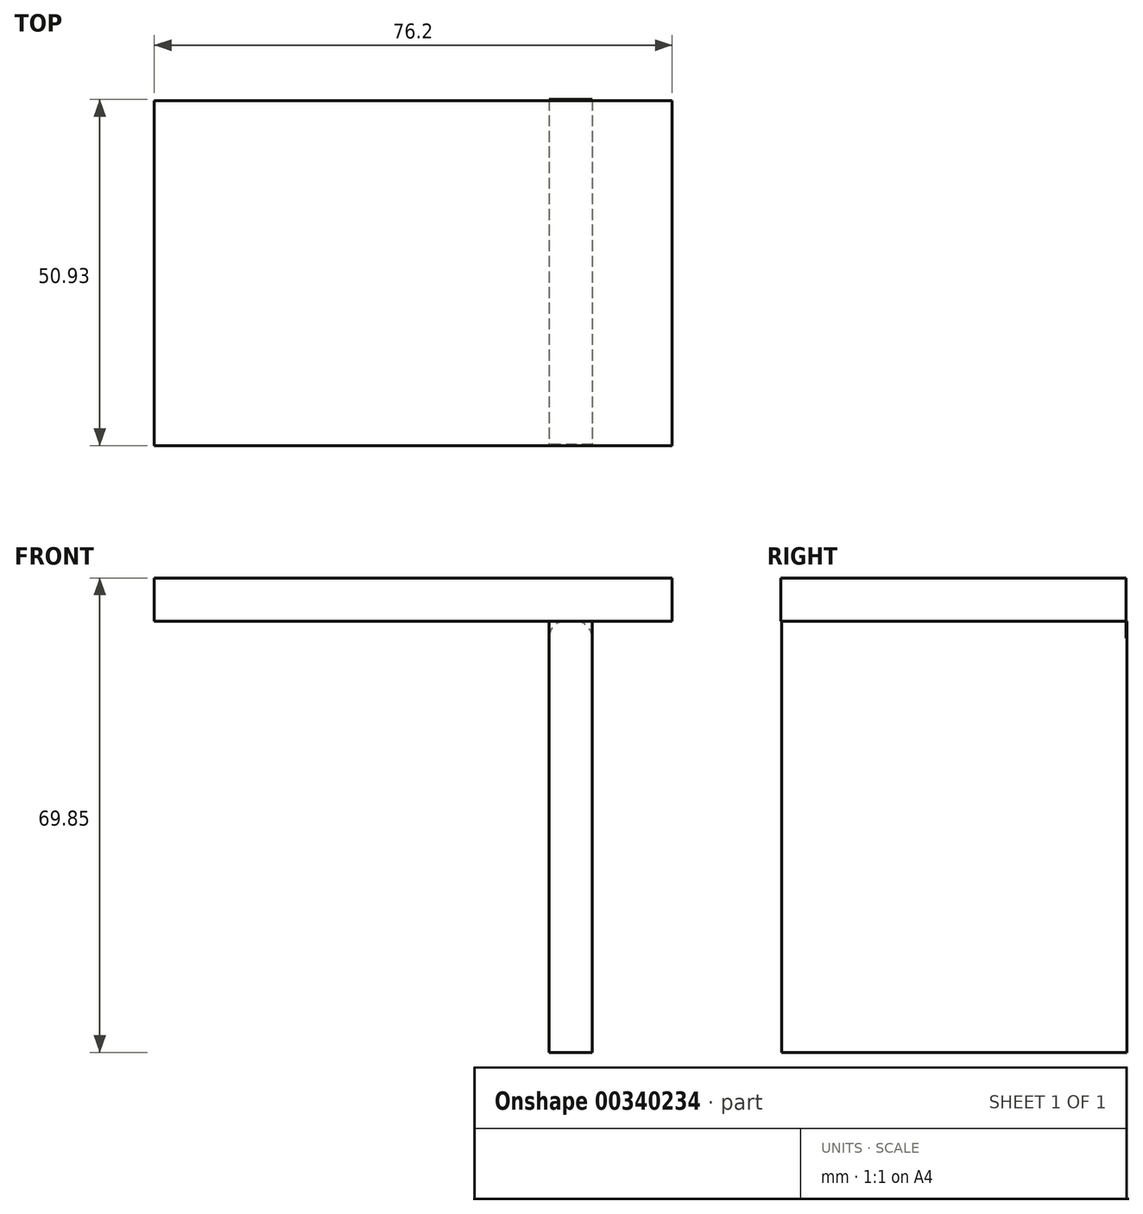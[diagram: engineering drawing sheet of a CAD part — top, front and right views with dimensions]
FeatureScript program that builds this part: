
annotation { "Feature Type Name" : "Feature", "Feature Type Description" : "" }
export const myFeature = defineFeature(function(context is Context, id is Id, definition is map)
    precondition{}
    {
        {
            var Q0;
            Q0=qCreatedBy(makeId("Top.planeOp"),FACE);
            var sketch = newSketch(context, id + "F0", { "sketchPlane" : qUnion([Q0])});
            skLineSegment(sketch, "E0.bottom", {"start": v(-37.07, 16.44) * mm, "end": v(39.13, 16.44) * mm});
            skLineSegment(sketch, "E0.top", {"start": v(-37.07, -34.36) * mm, "end": v(39.13, -34.36) * mm});
            skLineSegment(sketch, "E0.left", {"start": v(-37.07, 16.44) * mm, "end": v(-37.07, -34.36) * mm});
            skLineSegment(sketch, "E0.right", {"start": v(39.13, 16.44) * mm, "end": v(39.13, -34.36) * mm});
            skSolve(sketch);
        }
        {
            var Q0;
            Q0 = qSketchRegion(id + "F0", true);
            extrude(context, id + "F1", {"entities" : qUnion([Q0]), "depth" : 6.35 * mm});
        }
        {
            var Q0;
            Q0=qCreatedBy(makeId("Right.planeOp"),FACE);
            cPlane(context, id + "F2", {"entities" : qUnion([Q0]), "cplaneType" : CPlaneType.OFFSET, "offset" : 21 * mm, "width" : 150 * mm, "height" : 150 * mm});
        }
        {
            var Q0;
            Q0=qCreatedBy(id+"F2.planeOp",FACE);
            var sketch = newSketch(context, id + "F3", { "sketchPlane" : qUnion([Q0])});
            skLineSegment(sketch, "E1.bottom", {"start": v(16.57, 0) * mm, "end": v(-34.23, 0) * mm});
            skLineSegment(sketch, "E1.top", {"start": v(16.57, -63.5) * mm, "end": v(-34.23, -63.5) * mm});
            skLineSegment(sketch, "E1.left", {"start": v(16.57, 0) * mm, "end": v(16.57, -63.5) * mm});
            skLineSegment(sketch, "E1.right", {"start": v(-34.23, 0) * mm, "end": v(-34.23, -63.5) * mm});
            skSolve(sketch);
        }
        {
            var Q0;
            Q0 = qSketchRegion(id + "F3", true);
            extrude(context, id + "F4", {"entities" : qUnion([Q0]), "operationType" : NewBodyOperationType.ADD, "depth" : 6.35 * mm});
        }
        {
            var Q0;
            {var subQ0=sQuery(id+"F3.wireOp",EDGE,"E1.bottom");Q0=makeQuery(id+"F4.boolean.opBoolean","SPLIT",EDGE,{"disambiguationData":[topologyDisambiguationEdgeConnected([makeQuery(id+"F1.opExtrude","CAP_FACE",FACE,{"disambiguationData":[OSD([sQuery(id+"F0.wireOp",EDGE,"E0.bottom"),sQuery(id+"F0.wireOp",EDGE,"E0.top"),sQuery(id+"F0.wireOp",EDGE,"E0.left"),sQuery(id+"F0.wireOp",EDGE,"E0.right")])],"isStart":true})])],"derivedFrom":makeQuery(id+"F4.opExtrude","CAP_EDGE",EDGE,{"disambiguationData":[OSD([subQ0])],"isStart":true})});}
            var Q1;
            {var subQ0=sQuery(id+"F3.wireOp",EDGE,"E1.bottom");Q1=makeQuery(id+"F4.boolean.opBoolean","SPLIT",EDGE,{"disambiguationData":[topologyDisambiguationEdgeConnected([makeQuery(id+"F1.opExtrude","CAP_FACE",FACE,{"disambiguationData":[OSD([sQuery(id+"F0.wireOp",EDGE,"E0.bottom"),sQuery(id+"F0.wireOp",EDGE,"E0.top"),sQuery(id+"F0.wireOp",EDGE,"E0.left"),sQuery(id+"F0.wireOp",EDGE,"E0.right")])],"isStart":true})])],"derivedFrom":makeQuery(id+"F4.opExtrude","CAP_EDGE",EDGE,{"disambiguationData":[OSD([subQ0])],"isStart":false})});}
            fillet(context, id + "F5", {"entities" : qUnion([Q0, Q1]), "radius" : 2.5 * mm, "tangentPropagation" : true, "allowEdgeOverflow" : false});
        }
    });
